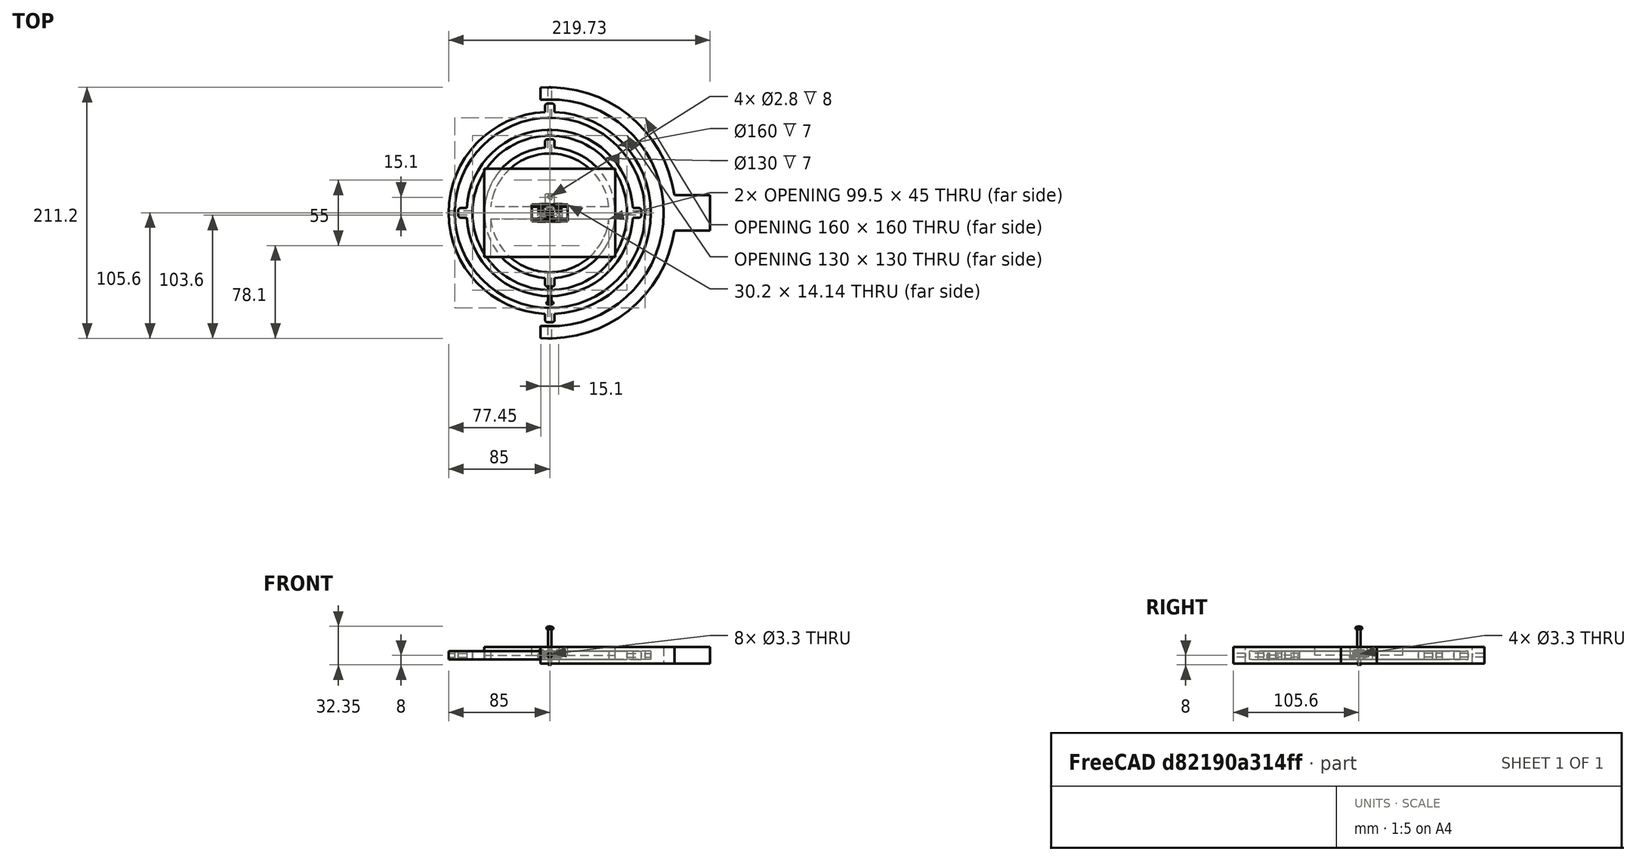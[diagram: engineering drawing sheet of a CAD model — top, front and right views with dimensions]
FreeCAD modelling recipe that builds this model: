
FCSTD DOCUMENT  (FreeCAD 1.1R40006 (Git))
Label: calibration_jig_v1
License: All rights reserved
LicenseURL: https://en.wikipedia.org/wiki/All_rights_reserved
objects: Part::Feature×61, App::Point×18, App::Link×17, App::FeaturePython×15, Sketcher::SketchObject×14, PartDesign::Pad×12, App::Part×11, PartDesign::Pocket×7, PartDesign::Body×6, Part::FeaturePython×4, PartDesign::Fillet×3, App::VarSet×1, PartDesign::Mirrored×1, Assembly::JointGroup×1, Assembly::AssemblyObject×1
note: 167 computed .brp shape members not serialized (recipe doc carries the construction recipe); baked Part::Feature solids carry a one-line shape summary decoded from their .brp

FEATURE [Part::Feature] Part__Feature001  label="PCB"
  shape: bbox 21 x 16 x 1.6 mm, 16 faces (baked)
FEATURE [Part::Feature] Part__Feature002  label="trou1"
  Placement = pos=(-8.89,-6.9,0) rot=(0,0,1;0rad)
  shape: bbox 1.8 x 1.8 x 1.8 mm, 8 faces (baked)
FEATURE [Part::Feature] Part__Feature003  label="trou002"
  Placement = pos=(-6.35,-6.9,0) rot=(0,0,1;0rad)
  shape: bbox 1.8 x 1.8 x 1.8 mm, 8 faces (baked)
FEATURE [Part::Feature] Part__Feature004  label="trou003"
  Placement = pos=(-3.81,-6.9,0) rot=(0,0,1;0rad)
  shape: bbox 1.8 x 1.8 x 1.8 mm, 8 faces (baked)
FEATURE [Part::Feature] Part__Feature005  label="trou004"
  Placement = pos=(-1.27,-6.9,0) rot=(0,0,1;0rad)
  shape: bbox 1.8 x 1.8 x 1.8 mm, 8 faces (baked)
FEATURE [Part::Feature] Part__Feature006  label="trou005"
  Placement = pos=(1.27,-6.9,0) rot=(0,0,1;0rad)
  shape: bbox 1.8 x 1.8 x 1.8 mm, 8 faces (baked)
FEATURE [Part::Feature] Part__Feature007  label="trou006"
  Placement = pos=(3.81,-6.9,0) rot=(0,0,1;0rad)
  shape: bbox 1.8 x 1.8 x 1.8 mm, 8 faces (baked)
FEATURE [Part::Feature] Part__Feature008  label="trou007"
  Placement = pos=(6.35,-6.9,0) rot=(0,0,1;0rad)
  shape: bbox 1.8 x 1.8 x 1.8 mm, 8 faces (baked)
FEATURE [Part::Feature] Part__Feature009  label="trou008"
  Placement = pos=(8.89,-6.9,0) rot=(0,0,1;0rad)
  shape: bbox 1.8 x 1.8 x 1.8 mm, 8 faces (baked)
FEATURE [Part::Feature] Part__Feature010  label="Text_VIN"
  Placement = pos=(-8.45,-3.45,-1.6) rot=(1,0,0;3.14159rad)
  shape: bbox 0.9349 x 0.8597 x 0.05 mm, 11 faces (baked)
FEATURE [Part::Feature] Part__Feature011  label="Text_VIN001"
  Placement = pos=(-8.45,-3.45,-1.6) rot=(1,0,0;3.14159rad)
  shape: bbox 0.9349 x 0.1223 x 0.05 mm, 6 faces (baked)
FEATURE [Part::Feature] Part__Feature012  label="Text_VIN002"
  Placement = pos=(-8.45,-3.45,-1.6) rot=(1,0,0;3.14159rad)
  shape: bbox 0.9349 x 0.7365 x 0.05 mm, 12 faces (baked)
FEATURE [App::Part] Text_VIN  label="Text_VIN003"
  Group = -> [Part__Feature010,Part__Feature011,Part__Feature012]
  Origin = -> Origin
FEATURE [App::Point] Origin001
  Role = Origin
FEATURE [Part::Feature] Part__Feature013  label="Text_3.3V"
  Placement = pos=(-5.81,-2.8,-1.6) rot=(1,0,0;3.14159rad)
  shape: bbox 0.9566 x 0.6115 x 0.05 mm, 32 faces (baked)
FEATURE [Part::Feature] Part__Feature014  label="Text_3.3V001"
  Placement = pos=(-5.81,-2.8,-1.6) rot=(1,0,0;3.14159rad)
  shape: bbox 0.1304 x 0.1304 x 0.05 mm, 6 faces (baked)
FEATURE [Part::Feature] Part__Feature015  label="Text_3.3V002"
  Placement = pos=(-5.81,-2.8,-1.6) rot=(1,0,0;3.14159rad)
  shape: bbox 0.9566 x 0.6115 x 0.05 mm, 32 faces (baked)
FEATURE [Part::Feature] Part__Feature016  label="Text_3.3V003"
  Placement = pos=(-5.81,-2.8,-1.6) rot=(1,0,0;3.14159rad)
  shape: bbox 0.9349 x 0.8597 x 0.05 mm, 11 faces (baked)
FEATURE [App::Part] Text_3_3V  label="Text_3.3V004"
  Group = -> [Part__Feature013,Part__Feature014,Part__Feature015,Part__Feature016]
  Origin = -> Origin002
FEATURE [App::Point] Origin003
  Role = Origin
FEATURE [Part::Feature] Part__Feature017  label="Text_GND"
  Placement = pos=(0.05,-8.35,-1.6) rot=(1,0,0;3.14159rad)
  shape: bbox 0.9675 x 0.8615 x 0.05 mm, 31 faces (baked)
FEATURE [Part::Feature] Part__Feature018  label="Text_GND001"
  Placement = pos=(0.05,-8.35,-1.6) rot=(1,0,0;3.14159rad)
  shape: bbox 0.9349 x 0.7365 x 0.05 mm, 12 faces (baked)
FEATURE [Part::Feature] Part__Feature019  label="Text_GND002"
  Placement = pos=(0.05,-8.35,-1.6) rot=(1,0,0;3.14159rad)
  shape: bbox 0.9349 x 0.7718 x 0.05 mm, 24 faces (baked)
FEATURE [App::Part] Text_GND  label="Text_GND003"
  Group = -> [Part__Feature017,Part__Feature018,Part__Feature019]
  Origin = -> Origin004
FEATURE [App::Point] Origin005
  Role = Origin
FEATURE [Part::Feature] Part__Feature020  label="Text_SCL"
  Placement = pos=(0.2,-8.65,-1.6) rot=(1,0,0;3.14159rad)
  shape: bbox 0.9675 x 0.7392 x 0.05 mm, 37 faces (baked)
FEATURE [Part::Feature] Part__Feature021  label="Text_SCL001"
  Placement = pos=(0.2,-8.65,-1.6) rot=(1,0,0;3.14159rad)
  shape: bbox 0.9675 x 0.8262 x 0.05 mm, 24 faces (baked)
FEATURE [Part::Feature] Part__Feature022  label="Text_SCL002"
  Placement = pos=(0.2,-8.65,-1.6) rot=(1,0,0;3.14159rad)
  shape: bbox 0.9349 x 0.5843 x 0.05 mm, 8 faces (baked)
FEATURE [App::Part] Text_SCL  label="Text_SCL003"
  Group = -> [Part__Feature020,Part__Feature021,Part__Feature022]
  Origin = -> Origin006
FEATURE [App::Point] Origin007
  Role = Origin
FEATURE [Part::Feature] Part__Feature023  label="Text_SDA"
  Placement = pos=(0.2,-8.45,-1.6) rot=(1,0,0;3.14159rad)
  shape: bbox 0.9675 x 0.7392 x 0.05 mm, 37 faces (baked)
FEATURE [Part::Feature] Part__Feature024  label="Text_SDA001"
  Placement = pos=(0.2,-8.45,-1.6) rot=(1,0,0;3.14159rad)
  shape: bbox 0.9349 x 0.7718 x 0.05 mm, 24 faces (baked)
FEATURE [Part::Feature] Part__Feature025  label="Text_SDA002"
  Placement = pos=(0.2,-8.45,-1.6) rot=(1,0,0;3.14159rad)
  shape: bbox 0.9349 x 0.8706 x 0.05 mm, 15 faces (baked)
FEATURE [App::Part] Text_SDA  label="Text_SDA003"
  Group = -> [Part__Feature023,Part__Feature024,Part__Feature025]
  Origin = -> Origin008
FEATURE [App::Point] Origin009
  Role = Origin
FEATURE [Part::Feature] Part__Feature026  label="Text_INT2"
  Placement = pos=(0,-8.4,-1.6) rot=(1,0,0;3.14159rad)
  shape: bbox 0.9349 x 0.1223 x 0.05 mm, 6 faces (baked)
FEATURE [Part::Feature] Part__Feature027  label="Text_INT003"
  Placement = pos=(0,-8.4,-1.6) rot=(1,0,0;3.14159rad)
  shape: bbox 0.9349 x 0.7365 x 0.05 mm, 12 faces (baked)
FEATURE [Part::Feature] Part__Feature028  label="Text_INT004"
  Placement = pos=(0,-8.4,-1.6) rot=(1,0,0;3.14159rad)
  shape: bbox 0.9349 x 0.7365 x 0.05 mm, 10 faces (baked)
FEATURE [Part::Feature] Part__Feature029  label="Text_INT005"
  Placement = pos=(0,-8.4,-1.6) rot=(1,0,0;3.14159rad)
  shape: bbox 0.9403 x 0.6209 x 0.05 mm, 24 faces (baked)
FEATURE [App::Part] Text_INT2  label="Text_INT006"
  Group = -> [Part__Feature026,Part__Feature027,Part__Feature028,Part__Feature029]
  Origin = -> Origin010
FEATURE [App::Point] Origin011
  Role = Origin
FEATURE [Part::Feature] Part__Feature030  label="Text_INT1"
  Placement = pos=(0,-8.6,-1.6) rot=(1,0,0;3.14159rad)
  shape: bbox 0.9349 x 0.1223 x 0.05 mm, 6 faces (baked)
FEATURE [Part::Feature] Part__Feature031  label="Text_INT007"
  Placement = pos=(0,-8.6,-1.6) rot=(1,0,0;3.14159rad)
  shape: bbox 0.9349 x 0.7365 x 0.05 mm, 12 faces (baked)
FEATURE [Part::Feature] Part__Feature032  label="Text_INT008"
  Placement = pos=(0,-8.6,-1.6) rot=(1,0,0;3.14159rad)
  shape: bbox 0.9349 x 0.7365 x 0.05 mm, 10 faces (baked)
FEATURE [Part::Feature] Part__Feature033  label="Text_INT009"
  Placement = pos=(0,-8.6,-1.6) rot=(1,0,0;3.14159rad)
  shape: bbox 0.9403 x 0.3451 x 0.05 mm, 11 faces (baked)
FEATURE [App::Part] Text_INT1  label="Text_INT010"
  Group = -> [Part__Feature030,Part__Feature031,Part__Feature032,Part__Feature033]
  Origin = -> Origin012
FEATURE [App::Point] Origin013
  Role = Origin
FEATURE [Part::Feature] Part__Feature034  label="Text_DRDY"
  Placement = pos=(0,-7.65,-1.6) rot=(1,0,0;3.14159rad)
  shape: bbox 0.9349 x 0.7718 x 0.05 mm, 24 faces (baked)
FEATURE [Part::Feature] Part__Feature035  label="Text_DRDY001"
  Placement = pos=(0,-7.65,-1.6) rot=(1,0,0;3.14159rad)
  shape: bbox 0.9349 x 0.8199 x 0.05 mm, 29 faces (baked)
FEATURE [Part::Feature] Part__Feature036  label="Text_DRDY002"
  Placement = pos=(0,-7.65,-1.6) rot=(1,0,0;3.14159rad)
  shape: bbox 0.9349 x 0.7718 x 0.05 mm, 24 faces (baked)
FEATURE [Part::Feature] Part__Feature037  label="Text_DRDY003"
  Placement = pos=(0,-7.65,-1.6) rot=(1,0,0;3.14159rad)
  shape: bbox 0.9349 x 0.8533 x 0.05 mm, 13 faces (baked)
FEATURE [App::Part] Text_DRDY  label="Text_DRDY004"
  Group = -> [Part__Feature034,Part__Feature035,Part__Feature036,Part__Feature037]
  Origin = -> Origin014
FEATURE [App::Point] Origin015
  Role = Origin
FEATURE [Part::Feature] Part__Feature038  label="R_0603_1608Metric"
  Placement = pos=(-2.45,-1.4,0) rot=(0,0,-1;1.5708rad)
  shape: bbox 0.8 x 1.6 x 0.45 mm, 26 faces (baked)
FEATURE [Part::Feature] Part__Feature039  label="R_0603_1608Metric001"
  Placement = pos=(-1.55,-4.1,0) rot=(0,0,1;0rad)
  shape: bbox 1.6 x 0.8 x 0.45 mm, 26 faces (baked)
FEATURE [Part::Feature] Part__Feature040  label="R_0603_1608Metric002"
  Placement = pos=(1.85,-4.1,0) rot=(0,0,1;3.14159rad)
  shape: bbox 1.6 x 0.8 x 0.45 mm, 26 faces (baked)
FEATURE [Part::Feature] Part__Feature041  label="R_0603_1608Metric003"
  Placement = pos=(2.7,-1.45,0) rot=(0,0,-1;1.5708rad)
  shape: bbox 0.8 x 1.6 x 0.45 mm, 26 faces (baked)
FEATURE [Part::Feature] Part__Feature042  label="C_0603_1608Metric001"
  Placement = pos=(4.2,3.55,0) rot=(0,0,-1;1.5708rad)
  shape: bbox 0.8 x 1.6 x 0.8 mm, 28 faces (baked)
FEATURE [Part::Feature] Part__Feature043  label="C_0603_1608Metric003"
  Placement = pos=(-3.85,5.25,0) rot=(0,0,-1;1.5708rad)
  shape: bbox 0.8 x 1.6 x 0.8 mm, 28 faces (baked)
FEATURE [Part::Feature] Part__Feature044  label="Corps002"
  Placement = pos=(-5.45,-0.65,0.1) rot=(0,0,-1;1.5708rad)
  shape: bbox 1.6 x 3.2 x 2 mm, 8 faces (baked)
FEATURE [Part::Feature] Part__Feature045  label="Corps001 (Mirror #1)"
  Placement = pos=(-1e-15,-1.3,0) rot=(0,0,1;3.14159rad)
  shape: bbox 1 x 0.6 x 1 mm, 8 faces (baked)
FEATURE [Part::Feature] Part__Feature046  label="C_0603_1608Metric004"
  Placement = pos=(-3.85,1.45,0) rot=(0,0,-1;1.5708rad)
  shape: bbox 0.8 x 1.6 x 0.8 mm, 28 faces (baked)
FEATURE [Part::Feature] Part__Feature047  label="C_0603_1608Metric005"
  Placement = pos=(-8.35,-3.5,0) rot=(0,0,1;3.14159rad)
  shape: bbox 1.6 x 0.8 x 0.8 mm, 28 faces (baked)
FEATURE [Part::Feature] Part__Feature048  label="Text_ITGMPU"
  Placement = pos=(-2.3,6.9,-1.6) rot=(0.707107,0.707107,0;3.14159rad)
  shape: bbox 1.034 x 1.161 x 0.05 mm, 31 faces (baked)
FEATURE [Part::Feature] Part__Feature049  label="Text_ITGMPU001"
  Placement = pos=(-2.3,6.9,-1.6) rot=(0.707107,0.707107,0;3.14159rad)
  shape: bbox 1.024 x 1.122 x 0.05 mm, 13 faces (baked)
FEATURE [Part::Feature] Part__Feature050  label="Text_ITGMPU002"
  Placement = pos=(-2.3,6.9,-1.6) rot=(0.707107,0.707107,0;3.14159rad)
  shape: bbox 0.4272 x 0.137 x 0.05 mm, 6 faces (baked)
FEATURE [Part::Feature] Part__Feature051  label="Text_ITGMPU003"
  Placement = pos=(-2.3,6.9,-1.6) rot=(0.707107,0.707107,0;3.14159rad)
  shape: bbox 0.7435 x 1.128 x 0.05 mm, 24 faces (baked)
FEATURE [Part::Feature] Part__Feature052  label="Text_ITGMPU004"
  Placement = pos=(-2.3,6.9,-1.6) rot=(0.707107,0.707107,0;3.14159rad)
  shape: bbox 0.4142 x 1.128 x 0.05 mm, 11 faces (baked)
FEATURE [Part::Feature] Part__Feature053  label="Text_ITGMPU005"
  Placement = pos=(-2.3,6.9,-1.6) rot=(0.707107,0.707107,0;3.14159rad)
  shape: bbox 0.4142 x 1.128 x 0.05 mm, 11 faces (baked)
FEATURE [App::Part] Text_ITGMPU  label="Text_ITGMPU006"
  Group = -> [Part__Feature048,Part__Feature049,Part__Feature050,Part__Feature051,Part__Feature052,Part__Feature053]
  Origin = -> Origin016
FEATURE [App::Point] Origin017
  Role = Origin
FEATURE [Part::Feature] Part__Feature054  label="SOT_23_5"
  Placement = pos=(-8.3,0.05,0) rot=(0,0,1;1.5708rad)
  shape: bbox 2.9 x 2.8 x 1.55 mm, 109 faces (baked)
FEATURE [Part::Feature] Part__Feature055  label="Text_XYZ"
  Placement = pos=(3.5,-0.7,0) rot=(0,0,1;0rad)
  shape: bbox 2.812 x 2.484 x 0.05 mm, 16 faces (baked)
FEATURE [Part::Feature] Part__Feature056  label="Text_XYZ001"
  Placement = pos=(3.5,-0.7,0) rot=(0,0,1;0rad)
  shape: bbox 1.038 x 0.6722 x 0.05 mm, 10 faces (baked)
FEATURE [Part::Feature] Part__Feature057  label="Text_XYZ002"
  Placement = pos=(3.5,-0.7,0) rot=(0,0,1;0rad)
  shape: bbox 1.038 x 0.6722 x 0.05 mm, 14 faces (baked)
FEATURE [Part::Feature] Part__Feature058  label="Text_XYZ003"
  Placement = pos=(3.5,-0.7,0) rot=(0,0,1;0rad)
  shape: bbox 1.038 x 0.6722 x 0.05 mm, 11 faces (baked)
FEATURE [App::Part] Text_XYZ  label="Text_XYZ004"
  Group = -> [Part__Feature055,Part__Feature056,Part__Feature057,Part__Feature058]
  Origin = -> Origin018
FEATURE [App::Point] Origin019
  Role = Origin
FEATURE [Part::Feature] Part__Feature059  label="LGA_14_3x5mm_P08mm_LayoutBorder1x6y"
  Placement = pos=(-1e-15,3.9,0) rot=(0,0,1;1.5708rad)
  shape: bbox 5 x 3 x 0.78 mm, 78 faces (baked)
FEATURE [Part::Feature] Part__Feature060  label="SOT_363_SC_70_6"
  Placement = pos=(0,-1.45,0) rot=(0,0,1;0rad)
  shape: bbox 2 x 2 x 1.05 mm, 118 faces (baked)
FEATURE [Part::Feature] Part__Feature061  label="Corps001"
  Placement = pos=(-5.45,-0.65,0) rot=(0,0,1;1.5708rad)
  shape: bbox 1 x 0.6 x 1 mm, 8 faces (baked)
FEATURE [App::Part] GY_511_LSM303DLHC
  Group = -> [Part__Feature001,Part__Feature002,Part__Feature003,Part__Feature004,Part__Feature005,Part__Feature006,Part__Feature007,Part__Feature008,Part__Feature009,Text_VIN,Text_3_3V,Text_GND,Text_SCL,Text_SDA,Text_INT2,Text_INT1,Text_DRDY,Part__Feature038,Part__Feature039,Part__Feature040,Part__Feature041,Part__Feature042,Part__Feature043,Part__Feature044,Part__Feature045,Part__Feature046,Part__Feature047,+6 more]
  Origin = -> Origin020
FEATURE [App::Point] Origin021
  Role = Origin
FEATURE [App::Point] Origin023
  Role = Origin
FEATURE [App::VarSet] VarSet
  Base_ring_base_diameter = 95.6
  Base_ring_connector_lenght = 8
  Base_ring_connector_scew = 3.3
  Base_ring_connector_width = 12
  Base_ring_depth = 7
  Base_ring_width = 10
  Base_second_ring_diameter = 130
  Base_sensor_base_diameter = 100
  Base_third_ring_diameter = 160
  expr: Base_ring_base_diameter = (Base_sensor_base_diameter + 6.6 * Base_ring_connector_width + 1.2 * Base_ring_width) / 2
  expr: Base_second_ring_diameter = Base_sensor_base_diameter + 1.5 * Base_ring_connector_width + 1.2 * Base_ring_width
  expr: Base_third_ring_diameter = Base_sensor_base_diameter + 4 * Base_ring_connector_width + 1.2 * Base_ring_width
FEATURE [Sketcher::SketchObject] Sketch
  ArcFitTolerance = 1e-06
  AttachmentSupport = -> [XY_Plane011]
  ExternalTypes = [0]
  FullyConstrained = true
  MakeInternals = false
  MapMode = 5
  expr: Constraints[2] = VarSet.Base_sensor_base_diameter
  expr: Constraints[3] = VarSet.Base_sensor_base_diameter + VarSet.Base_ring_width
  sketch-geometry (2):
    g0: Circle CenterX=0 CenterY=0 CenterZ=0 NormalX=0 NormalY=0 NormalZ=1 AngleXU=0 Radius=55
    g1: Circle CenterX=0 CenterY=0 CenterZ=0 NormalX=0 NormalY=0 NormalZ=1 AngleXU=0 Radius=50
  constraints (5):
    c: Coincident(g0,g-1)
    c: PointOnObject(g1,g-2)
    c: Diameter(g1) = 100
    c: Diameter(g0) = 110
    c: PointOnObject(g1,g-1)
FEATURE [PartDesign::Pad] Pad002
  Direction = (0,0,1)
  Length = 7
  Length2 = 10
  Midplane = true
  Profile = -> Sketch
  ReferenceAxis = -> Sketch [N_Axis]
  Refine = true
  Suppressed = false
  Type = 0
  expr: Length = VarSet.Base_ring_depth
FEATURE [Sketcher::SketchObject] Sketch069
  ArcFitTolerance = 1e-06
  AttachmentSupport = -> [XY_Plane011]
  ExternalTypes = [0]
  FullyConstrained = true
  MakeInternals = false
  MapMode = 5
  expr: Constraints[10] = VarSet.Base_sensor_base_diameter / 2
  expr: Constraints[7] = VarSet.Base_ring_connector_lenght
  expr: Constraints[8] = VarSet.Base_ring_connector_width
  sketch-geometry (4):
    g0: LineSegment StartX=-4 StartY=62 StartZ=0 EndX=-4 EndY=50 EndZ=0
    g1: LineSegment StartX=-4 StartY=50 StartZ=0 EndX=4 EndY=50 EndZ=0
    g2: LineSegment StartX=4 StartY=50 StartZ=0 EndX=4 EndY=62 EndZ=0
    g3: LineSegment StartX=4 StartY=62 StartZ=0 EndX=-4 EndY=62 EndZ=0
  constraints (11):
    c: Coincident(g0,g1)
    c: Coincident(g1,g2)
    c: Coincident(g2,g3)
    c: Coincident(g3,g0)
    c: Vertical(g0)
    c: Vertical(g2)
    c: Horizontal(g1)
    c: Distance(g0,g2) = 8
    c: Distance(g1,g3) = 12
    c: Symmetric(g0,g2,g-2)
    c: DistanceY(g-1,g1) = 50
FEATURE [PartDesign::Pad] Pad003
  BaseFeature = -> Pad002
  Direction = (0,0,1)
  Length = 7
  Length2 = 10
  Midplane = true
  Profile = -> Sketch069
  ReferenceAxis = -> Sketch069 [N_Axis]
  Refine = true
  Suppressed = false
  Type = 0
  expr: Length = VarSet.Base_ring_depth
FEATURE [PartDesign::Mirrored] Mirrored
  BaseFeature = -> Pad003
  MirrorPlane = -> Sketch069 [H_Axis]
  Originals = -> [Pad003]
  Refine = true
  Suppressed = false
  TransformMode = 0
FEATURE [App::Point] Origin087
  Role = Origin
FEATURE [Sketcher::SketchObject] Sketch071
  ArcFitTolerance = 1e-06
  AttachmentSupport = -> [XY_Plane046]
  ExternalTypes = [0]
  FullyConstrained = true
  MakeInternals = false
  MapMode = 5
  expr: Constraints[13] = VarSet.Base_ring_connector_width
  expr: Constraints[14] = VarSet.Base_ring_connector_lenght
  expr: Constraints[2] = VarSet.Base_second_ring_diameter
  expr: Constraints[3] = VarSet.Base_second_ring_diameter + VarSet.Base_ring_width
  sketch-geometry (10):
    g0: Circle CenterX=0 CenterY=0 CenterZ=0 NormalX=0 NormalY=0 NormalZ=1 AngleXU=0 Radius=70
    g1: Circle CenterX=0 CenterY=0 CenterZ=0 NormalX=0 NormalY=0 NormalZ=1 AngleXU=0 Radius=65
    g2: LineSegment StartX=65 StartY=4 StartZ=0 EndX=65 EndY=-4 EndZ=0
    g3: LineSegment StartX=65 StartY=-4 StartZ=0 EndX=77 EndY=-4 EndZ=0
    g4: LineSegment StartX=77 StartY=-4 StartZ=0 EndX=77 EndY=4 EndZ=0
    g5: LineSegment StartX=77 StartY=4 StartZ=0 EndX=65 EndY=4 EndZ=0
    g6: LineSegment StartX=-77 StartY=4 StartZ=0 EndX=-65 EndY=4 EndZ=0
    g7: LineSegment StartX=-65 StartY=4 StartZ=0 EndX=-65 EndY=-4 EndZ=0
    g8: LineSegment StartX=-65 StartY=-4 StartZ=0 EndX=-77 EndY=-4 EndZ=0
    g9: LineSegment StartX=-77 StartY=-4 StartZ=0 EndX=-77 EndY=4 EndZ=0
  constraints (26):
    c: Coincident(g0,g-1)
    c: Coincident(g1,g0)
    c: Diameter(g1) = 130
    c: Diameter(g0) = 140
    c: Coincident(g2,g3)
    c: Coincident(g3,g4)
    c: Coincident(g4,g5)
    c: Coincident(g5,g2)
    c: Vertical(g4)
    c: Horizontal(g3)
    c: Horizontal(g5)
    c: Symmetric(g2,g2,g-1)
    c: Tangent(g2,g1)
    c: DistanceX(g2,g3) = 12
    c: DistanceY(g3,g4) = 8
    c: Coincident(g7,g8)
    c: Coincident(g8,g9)
    c: Coincident(g9,g6)
    c: Coincident(g6,g7)
    c: Vertical(g9)
    c: Horizontal(g8)
    c: Horizontal(g6)
    c: Equal(g3,g8)
    c: Equal(g9,g4)
    c: Symmetric(g7,g6,g-1)
    c: Tangent(g7,g1)
FEATURE [PartDesign::Pad] Pad004
  Direction = (0,0,1)
  Length = 7
  Length2 = 10
  Midplane = true
  Profile = -> Sketch071 [Edge1,Edge2]
  ReferenceAxis = -> Sketch071 [N_Axis]
  Refine = true
  Suppressed = false
  Type = 0
  expr: Length = VarSet.Base_ring_depth
FEATURE [PartDesign::Pad] Pad005
  BaseFeature = -> Pad004
  Direction = (0,0,1)
  Length = 7
  Length2 = 10
  Midplane = true
  Profile = -> Sketch071 [Edge7,Edge8,Edge9,Edge10,Edge3,Edge6,Edge5,Edge4]
  ReferenceAxis = -> Sketch071 [N_Axis]
  Refine = true
  Suppressed = false
  Type = 0
  expr: Length = VarSet.Base_ring_depth
FEATURE [Sketcher::SketchObject] Sketch073
  ArcFitTolerance = 1e-06
  AttachmentSupport = -> [XZ_Plane046]
  ExternalTypes = [0]
  FullyConstrained = true
  MakeInternals = false
  MapMode = 5
  Placement = pos=(0,0,0) rot=(1,0,0;1.5708rad)
  expr: Constraints[1] = VarSet.Base_ring_connector_scew
  sketch-geometry (1):
    g0: Circle CenterX=0 CenterY=0 CenterZ=0 NormalX=0 NormalY=0 NormalZ=1 AngleXU=0 Radius=1.65
  constraints (2):
    c: Coincident(g0,g-1)
    c: Diameter(g0) = 3.3
FEATURE [PartDesign::Pocket] Pocket003
  BaseFeature = -> Pad005
  Direction = (0,1,-2e-16)
  Length = 5
  Length2 = 5
  Midplane = true
  Profile = -> Sketch073
  ReferenceAxis = -> Sketch073 [N_Axis]
  Refine = true
  Suppressed = false
  Type = 1
FEATURE [App::Point] Origin089
  Role = Origin
FEATURE [Sketcher::SketchObject] Sketch074
  ArcFitTolerance = 1e-06
  AttachmentSupport = -> [XY_Plane047]
  ExternalTypes = [0]
  FullyConstrained = true
  MakeInternals = false
  MapMode = 5
  expr: Constraints[12] = VarSet.Base_ring_connector_lenght
  expr: Constraints[13] = VarSet.Base_ring_connector_width
  expr: Constraints[1] = VarSet.Base_third_ring_diameter
  expr: Constraints[23] = VarSet.Base_ring_connector_width
  expr: Constraints[24] = VarSet.Base_ring_connector_lenght
  expr: Constraints[2] = VarSet.Base_third_ring_diameter + VarSet.Base_ring_width
  sketch-geometry (10):
    g0: Circle CenterX=0 CenterY=0 CenterZ=0 NormalX=0 NormalY=0 NormalZ=1 AngleXU=0 Radius=85
    g1: Circle CenterX=0 CenterY=0 CenterZ=0 NormalX=0 NormalY=0 NormalZ=1 AngleXU=0 Radius=80
    g2: LineSegment StartX=-4 StartY=92 StartZ=0 EndX=-4 EndY=80 EndZ=0
    g3: LineSegment StartX=-4 StartY=80 StartZ=0 EndX=4 EndY=80 EndZ=0
    g4: LineSegment StartX=4 StartY=80 StartZ=0 EndX=4 EndY=92 EndZ=0
    g5: LineSegment StartX=4 StartY=92 StartZ=0 EndX=-4 EndY=92 EndZ=0
    g6: LineSegment StartX=-4 StartY=-80 StartZ=0 EndX=-4 EndY=-92 EndZ=0
    g7: LineSegment StartX=-4 StartY=-92 StartZ=0 EndX=4 EndY=-92 EndZ=0
    g8: LineSegment StartX=4 StartY=-92 StartZ=0 EndX=4 EndY=-80 EndZ=0
    g9: LineSegment StartX=4 StartY=-80 StartZ=0 EndX=-4 EndY=-80 EndZ=0
  constraints (26):
    c: Coincident(g1,g0)
    c: Diameter(g1) = 160
    c: Diameter(g0) = 170
    c: Coincident(g0,g-1)
    c: Coincident(g2,g3)
    c: Coincident(g3,g4)
    c: Coincident(g4,g5)
    c: Coincident(g5,g2)
    c: Vertical(g2)
    c: Vertical(g4)
    c: Horizontal(g5)
    c: Symmetric(g2,g3,g-2)
    c: DistanceX(g2,g3) = 8
    c: DistanceY(g3,g4) = 12
    c: Tangent(g3,g1)
    c: Coincident(g6,g7)
    c: Coincident(g7,g8)
    c: Coincident(g8,g9)
    c: Coincident(g9,g6)
    c: Vertical(g6)
    c: Vertical(g8)
    c: Horizontal(g9)
    c: Symmetric(g7,g6,g-2)
    c: DistanceY(g6,g6) = 12
    c: DistanceX(g6,g8) = 8
    c: Tangent(g9,g1)
FEATURE [Sketcher::SketchObject] Sketch075
  ArcFitTolerance = 1e-06
  AttachmentSupport = -> [XZ_Plane047]
  ExternalTypes = [0]
  FullyConstrained = true
  MakeInternals = false
  MapMode = 5
  Placement = pos=(0,0,0) rot=(1,0,0;1.5708rad)
  expr: Constraints[1] = VarSet.Base_ring_connector_scew
  sketch-geometry (1):
    g0: Circle CenterX=0 CenterY=0 CenterZ=0 NormalX=0 NormalY=0 NormalZ=1 AngleXU=0 Radius=1.65
  constraints (2):
    c: Coincident(g0,g-1)
    c: Diameter(g0) = 3.3
FEATURE [Sketcher::SketchObject] Sketch076
  ArcFitTolerance = 1e-06
  AttachmentSupport = -> [YZ_Plane047]
  ExternalTypes = [0]
  FullyConstrained = true
  MakeInternals = false
  MapMode = 5
  Placement = pos=(0,0,0) rot=(0.57735,0.57735,0.57735;2.0944rad)
  expr: Constraints[1] = VarSet.Base_ring_connector_scew
  sketch-geometry (1):
    g0: Circle CenterX=0 CenterY=0 CenterZ=0 NormalX=0 NormalY=0 NormalZ=1 AngleXU=0 Radius=1.65
  constraints (2):
    c: Coincident(g0,g-1)
    c: Diameter(g0) = 3.3
FEATURE [PartDesign::Pad] Pad006
  Direction = (0,0,1)
  Length = 7
  Length2 = 10
  Midplane = true
  Profile = -> Sketch074 [Edge2,Edge1]
  ReferenceAxis = -> Sketch074 [N_Axis]
  Refine = true
  Suppressed = false
  Type = 0
  expr: Length = VarSet.Base_ring_depth
FEATURE [PartDesign::Pad] Pad007
  BaseFeature = -> Pad006
  Direction = (0,0,1)
  Length = 7
  Length2 = 10
  Midplane = true
  Profile = -> Sketch074 [Edge4,Edge3,Edge5,Edge6,Edge10,Edge7,Edge8,Edge9]
  ReferenceAxis = -> Sketch074 [N_Axis]
  Refine = true
  Suppressed = false
  Type = 0
  expr: Length = VarSet.Base_ring_depth
FEATURE [PartDesign::Pocket] Pocket004
  BaseFeature = -> Pad007
  Direction = (-1,0,0)
  Length = 5
  Length2 = 5
  Midplane = true
  Profile = -> Sketch076
  ReferenceAxis = -> Sketch076 [N_Axis]
  Refine = true
  Suppressed = false
  Type = 1
FEATURE [PartDesign::Pocket] Pocket005
  BaseFeature = -> Pocket004
  Direction = (0,1,-2e-16)
  Length = 5
  Length2 = 5
  Midplane = true
  Profile = -> Sketch075
  ReferenceAxis = -> Sketch075 [N_Axis]
  Refine = true
  Suppressed = false
  Type = 1
FEATURE [App::Point] Origin091
  Role = Origin
FEATURE [Sketcher::SketchObject] Sketch077
  ArcFitTolerance = 1e-06
  AttachmentSupport = -> [XY_Plane048]
  ExternalTypes = [0]
  FullyConstrained = true
  MakeInternals = false
  MapMode = 5
  expr: Constraints[11] = 3 * VarSet.Base_ring_width
  expr: Constraints[20] = VarSet.Base_ring_base_diameter
  expr: Constraints[7] = VarSet.Base_ring_width
  sketch-geometry (15):
    g0: ArcOfCircle CenterX=0.199246 CenterY=2.76e-14 CenterZ=0 NormalX=0 NormalY=0 NormalZ=1 AngleXU=0 Radius=105.6 StartAngle=0.142528 EndAngle=1.64852
    g1: ArcOfCircle CenterX=0.199246 CenterY=2.05388e-11 CenterZ=0 NormalX=0 NormalY=0 NormalZ=1 AngleXU=0 Radius=105.6 StartAngle=4.63467 EndAngle=6.14066
    g2: LineSegment StartX=-8 StartY=105.281 StartZ=0 EndX=-8 EndY=95.2812 EndZ=0
    g3: LineSegment StartX=-8 StartY=-105.281 StartZ=0 EndX=-8 EndY=-95.2812 EndZ=0
    g4: LineSegment [constr] StartX=-8 StartY=-105.281 StartZ=0 EndX=-8 EndY=105.281 EndZ=0
    g5: LineSegment StartX=104.728 StartY=-15 StartZ=0 EndX=134.728 EndY=-15 EndZ=0
    g6: LineSegment StartX=134.728 StartY=-15 StartZ=0 EndX=134.728 EndY=15 EndZ=0
    g7: LineSegment StartX=134.728 StartY=15 StartZ=0 EndX=104.728 EndY=15 EndZ=0
    g8: LineSegment [constr] StartX=134.728 StartY=-15 StartZ=0 EndX=104.728 EndY=-15 EndZ=0
    g9: LineSegment [constr] StartX=134.728 StartY=15 StartZ=0 EndX=104.728 EndY=15 EndZ=0
    g10: ArcOfCircle CenterX=0.199246 CenterY=2.76e-14 CenterZ=0 NormalX=0 NormalY=0 NormalZ=1 AngleXU=0 Radius=95.6 StartAngle=4.79408 EndAngle=7.77229
    g11: LineSegment StartX=-8 StartY=-95.2812 StartZ=0 EndX=8 EndY=-95.2812 EndZ=0
    g12: LineSegment StartX=-8 StartY=95.2812 StartZ=0 EndX=8 EndY=95.2812 EndZ=0
    g13: LineSegment [constr] StartX=8 StartY=95.2812 StartZ=0 EndX=8 EndY=-95.2812 EndZ=0
    g14: LineSegment [constr] StartX=104.728 StartY=-15 StartZ=0 EndX=104.728 EndY=15 EndZ=0
  constraints (40):
    c: Coincident(g2,g0)
    c: Coincident(g3,g1)
    c: Coincident(g4,g1)
    c: Coincident(g4,g0)
    c: Vertical(g4)
    c: PointOnObject(g2,g4)
    c: Distance(g4,g-2) = 8
    c: DistanceY(g2,g0) = 10
    c: Equal(g3,g2)
    c: Coincident(g5,g6)
    c: Coincident(g6,g7)
    c: DistanceY(g5,g6) = 30
    c: Distance(g8,g5) = 30
    c: Horizontal(g5)
    c: Coincident(g1,g5)
    c: Horizontal(g7)
    c: Coincident(g0,g7)
    c: Coincident(g8,g5)
    c: Coincident(g9,g6)
    c: Coincident(g10,g0)
    c: Radius(g10) = 95.6
    c: Coincident(g11,g3)
    c: Coincident(g11,g10)
    c: Horizontal(g11)
    c: Coincident(g12,g2)
    c: Coincident(g12,g10)
    c: Horizontal(g12)
    c: Coincident(g13,g10)
    c: Coincident(g13,g10)
    c: Vertical(g13)
    c: Distance(g13,g4) = 16
    c: Symmetric(g5,g6,g-1)
    c: Coincident(g8,g1)
    c: Coincident(g14,g1)
    c: Coincident(g14,g0)
    c: Vertical(g14)
    c: Coincident(g9,g0)
    c: Symmetric(g2,g3,g-1)
    c: Distance(g0,g10) = 10
    c: Equal(g1,g0)
FEATURE [PartDesign::Pad] Pad008
  Direction = (0,0,1)
  Length = 14
  Length2 = 10
  Midplane = true
  Profile = -> Sketch077
  ReferenceAxis = -> Sketch077 [N_Axis]
  Refine = true
  Suppressed = false
  Type = 0
  expr: Length = 2 * VarSet.Base_ring_depth
FEATURE [App::Point] Origin093
  Role = Origin
FEATURE [Sketcher::SketchObject] Sketch078
  ArcFitTolerance = 1e-06
  AttachmentSupport = -> [XY_Plane049]
  ExternalTypes = [0]
  FullyConstrained = true
  MakeInternals = false
  MapMode = 5
  expr: Constraints[20] = 2.02 * VarSet.Base_ring_depth
  expr: Constraints[21] = 3.02 * VarSet.Base_ring_width
  sketch-geometry (10):
    g0: LineSegment StartX=-15.1 StartY=7.07 StartZ=0 EndX=-15.1 EndY=-7.07 EndZ=0
    g1: LineSegment StartX=-15.1 StartY=-7.07 StartZ=0 EndX=15.1 EndY=-7.07 EndZ=0
    g2: LineSegment StartX=15.1 StartY=-7.07 StartZ=0 EndX=15.1 EndY=7.07 EndZ=0
    g3: LineSegment StartX=15.1 StartY=7.07 StartZ=0 EndX=-15.1 EndY=7.07 EndZ=0
    g4: GeomPoint [constr] X=0 Y=0 Z=0
    g5: LineSegment StartX=-55.1 StartY=37.07 StartZ=0 EndX=-55.1 EndY=-37.07 EndZ=0
    g6: LineSegment StartX=-55.1 StartY=-37.07 StartZ=0 EndX=55.1 EndY=-37.07 EndZ=0
    g7: LineSegment StartX=55.1 StartY=-37.07 StartZ=0 EndX=55.1 EndY=37.07 EndZ=0
    g8: LineSegment StartX=55.1 StartY=37.07 StartZ=0 EndX=-55.1 EndY=37.07 EndZ=0
    g9: GeomPoint [constr] X=0 Y=0 Z=0
  constraints (24):
    c: Coincident(g0,g1)
    c: Coincident(g1,g2)
    c: Coincident(g2,g3)
    c: Coincident(g3,g0)
    c: Vertical(g0)
    c: Vertical(g2)
    c: Horizontal(g1)
    c: Horizontal(g3)
    c: Symmetric(g2,g0,g4)
    c: Coincident(g4,g-1)
    c: Coincident(g5,g6)
    c: Coincident(g6,g7)
    c: Coincident(g7,g8)
    c: Coincident(g8,g5)
    c: Vertical(g5)
    c: Vertical(g7)
    c: Horizontal(g6)
    c: Horizontal(g8)
    c: Symmetric(g7,g5,g9)
    c: Coincident(g9,g4)
    c: DistanceY(g1,g2) = 14.14
    c: DistanceX(g0,g2) = 30.2
    c: DistanceX(g5,g0) = 40
    c: DistanceY(g0,g5) = 30
FEATURE [PartDesign::Pad] Pad009
  Direction = (0,0,1)
  Length = 7
  Length2 = 10
  Profile = -> Sketch078
  ReferenceAxis = -> Sketch078 [N_Axis]
  Refine = true
  Suppressed = false
  Type = 0
  expr: Length = VarSet.Base_ring_depth
FEATURE [PartDesign::Body] Body024  label="base"
  AllowCompound = false
  Group = -> [Sketch078,Pad009]
  Origin = -> Origin092
  Tip = -> Pad009
FEATURE [Sketcher::SketchObject] Sketch079
  ArcFitTolerance = 1e-06
  AttachmentSupport = -> [XZ_Plane048]
  ExternalTypes = [0]
  FullyConstrained = true
  MakeInternals = false
  MapMode = 5
  Placement = pos=(0,0,0) rot=(1,0,0;1.5708rad)
  expr: Constraints[1] = VarSet.Base_ring_connector_scew
  sketch-geometry (1):
    g0: Circle CenterX=0 CenterY=0 CenterZ=0 NormalX=0 NormalY=0 NormalZ=1 AngleXU=0 Radius=1.65
  constraints (2):
    c: Coincident(g0,g-1)
    c: Diameter(g0) = 3.3
FEATURE [PartDesign::Pocket] Pocket006
  BaseFeature = -> Pad008
  Direction = (0,1,-2e-16)
  Length = 5
  Length2 = 5
  Midplane = true
  Profile = -> Sketch079
  ReferenceAxis = -> Sketch079 [N_Axis]
  Refine = true
  Suppressed = false
  Type = 1
FEATURE [PartDesign::Body] Body023  label="base_outside"
  AllowCompound = false
  Group = -> [Sketch077,Pad008,Sketch079,Pocket006]
  Origin = -> Origin090
  Tip = -> Pocket006
FEATURE [App::Point] Origin095
  Role = Origin
FEATURE [Sketcher::SketchObject] Sketch080
  ArcFitTolerance = 1e-06
  AttachmentSupport = -> [XY_Plane050]
  ExternalTypes = [0]
  FullyConstrained = true
  MakeInternals = false
  MapMode = 5
  expr: Constraints[2] = VarSet.Base_ring_connector_scew
  sketch-geometry (2):
    g0: Circle CenterX=0 CenterY=0 CenterZ=0 NormalX=0 NormalY=0 NormalZ=1 AngleXU=0 Radius=1.65
    g1: Circle CenterX=0 CenterY=0 CenterZ=0 NormalX=0 NormalY=0 NormalZ=1 AngleXU=0 Radius=3.65
  constraints (4):
    c: Coincident(g0,g-1)
    c: Coincident(g1,g0)
    c: Diameter(g0) = 3.3
    c: Distance(g0,g1) = 2
FEATURE [PartDesign::Pad] Pad010
  Direction = (0,0,1)
  Length = 2
  Length2 = 10
  Midplane = true
  Profile = -> Sketch080
  ReferenceAxis = -> Sketch080 [N_Axis]
  Refine = true
  Suppressed = false
  Type = 0
FEATURE [PartDesign::Body] Body025  label="space"
  AllowCompound = false
  Group = -> [Sketch080,Pad010]
  Origin = -> Origin094
  Tip = -> Pad010
FEATURE [App::Point] Origin097
  Role = Origin
FEATURE [App::Link] base  label="base001"
  LinkedObject = -> Body024
FEATURE [App::FeaturePython] GroundedJoint  # Assembly grounded joint (typed FeaturePython)
  ObjectToGround = -> base
FEATURE [App::Link] base_outside  label="base_outside001"
  LinkPlacement = pos=(-2.6e-15,14.07,134.728) rot=(0.57735,0.57735,-0.57735;2.0944rad)
  LinkedObject = -> Body023
  Placement = pos=(-2.6e-15,14.07,134.728) rot=(0.57735,0.57735,-0.57735;2.0944rad)
FEATURE [App::Link] space  label="space001"
  LinkPlacement = pos=(94.4373,14.07,134.728) rot=(0.707107,0,-0.707107;3.14159rad)
  LinkedObject = -> Body025
  Placement = pos=(94.4373,14.07,134.728) rot=(0.707107,0,-0.707107;3.14159rad)
FEATURE [App::Link] third_circle  label="third_circle001"
  LinkPlacement = pos=(1.43729,14.07,134.728) rot=(0.57735,0.57735,-0.57735;2.0944rad)
  LinkedObject = -> Body022
  Placement = pos=(1.43729,14.07,134.728) rot=(0.57735,0.57735,-0.57735;2.0944rad)
FEATURE [App::Link] space001  label="space006"
  LinkPlacement = pos=(1.43729,14.07,213.22) rot=(0,0,1;0rad)
  LinkedObject = -> Body025
  Placement = pos=(1.43729,14.07,213.22) rot=(0,0,1;0rad)
FEATURE [App::Link] space002  label="space003"
  LinkPlacement = pos=(80.5115,1.7298,121.104) rot=(-0.384867,0.643615,0.661542;1.87625rad)
  LinkedObject = -> Body025
  Placement = pos=(80.5115,1.7298,121.104) rot=(-0.384867,0.643615,0.661542;1.87625rad)
FEATURE [App::Link] space003  label="space004"
  LinkPlacement = pos=(-62.0526,14.07,135.22) rot=(0,1,0;4.71239rad)
  LinkedObject = -> Body025
  Placement = pos=(-62.0526,14.07,135.22) rot=(0,1,0;4.71239rad)
FEATURE [App::Link] second_cicle  label="second_cicle001"
  LinkPlacement = pos=(1.43729,14.07,135.22) rot=(0.57735,0.57735,0.57735;4.18879rad)
  LinkedObject = -> Body021
  Placement = pos=(1.43729,14.07,135.22) rot=(0.57735,0.57735,0.57735;4.18879rad)
FEATURE [App::Link] first_circle  label="first_circle001"
  LinkPlacement = pos=(0.947386,14.07,135.22) rot=(-0.57735,0.57735,-0.57735;4.18879rad)
  LinkedObject = -> Body
  Placement = pos=(0.947386,14.07,135.22) rot=(-0.57735,0.57735,-0.57735;4.18879rad)
FEATURE [App::Link] space004  label="space005"
  LinkPlacement = pos=(89.3064,-1.573,115.544) rot=(0.56245,0.669832,-0.484742;3.28422rad)
  LinkedObject = -> Body025
  Placement = pos=(89.3064,-1.573,115.544) rot=(0.56245,0.669832,-0.484742;3.28422rad)
FEATURE [Sketcher::SketchObject] Sketch081  label="sensor_base"
  ArcFitTolerance = 1e-06
  AttachmentSupport = -> [XY_Plane011]
  ExternalTypes = [0]
  FullyConstrained = true
  MakeInternals = false
  MapMode = 5
  expr: Constraints[20] = VarSet.Base_sensor_base_diameter * 1.1
  sketch-geometry (18):
    g0: Circle CenterX=7.55 CenterY=2.4 CenterZ=0 NormalX=0 NormalY=0 NormalZ=1 AngleXU=0 Radius=1.4
    g1: Circle CenterX=-7.55 CenterY=2.4 CenterZ=0 NormalX=0 NormalY=0 NormalZ=1 AngleXU=0 Radius=1.4
    g2: Circle CenterX=-7.55 CenterY=2.4 CenterZ=0 NormalX=0 NormalY=0 NormalZ=1 AngleXU=0 Radius=2.2
    g3: Circle CenterX=7.55 CenterY=2.4 CenterZ=0 NormalX=0 NormalY=0 NormalZ=1 AngleXU=0 Radius=2.2
    g4: GeomPoint X=-1e-16 Y=2.4 Z=0
    g5: LineSegment [constr] StartX=-1e-16 StartY=2.4 StartZ=0 EndX=-1e-16 EndY=-1.6 EndZ=0
    g6: LineSegment StartX=-55 StartY=-5 StartZ=0 EndX=55 EndY=-5 EndZ=0
    g7: LineSegment StartX=55 StartY=5 StartZ=0 EndX=-55 EndY=5 EndZ=0
    g8: Circle CenterX=0 CenterY=-2 CenterZ=0 NormalX=0 NormalY=0 NormalZ=1 AngleXU=0 Radius=2.2
    g9: LineSegment StartX=-55 StartY=5 StartZ=0 EndX=-55 EndY=-5 EndZ=0
    g10: LineSegment StartX=55 StartY=-5 StartZ=0 EndX=55 EndY=5 EndZ=0
    g11: Circle CenterX=0 CenterY=-2 CenterZ=0 NormalX=0 NormalY=0 NormalZ=1 AngleXU=0 Radius=1.4
    g12: Circle CenterX=0 CenterY=13.1 CenterZ=0 NormalX=0 NormalY=0 NormalZ=1 AngleXU=0 Radius=1.4
    g13: Circle CenterX=0 CenterY=13.1 CenterZ=0 NormalX=0 NormalY=0 NormalZ=1 AngleXU=0 Radius=2.2
    g14: LineSegment StartX=-4 StartY=16 StartZ=0 EndX=-4 EndY=4 EndZ=0
    g15: LineSegment StartX=-4 StartY=4 StartZ=0 EndX=4 EndY=4 EndZ=0
    g16: LineSegment StartX=4 StartY=4 StartZ=0 EndX=4 EndY=16 EndZ=0
    g17: LineSegment StartX=4 StartY=16 StartZ=0 EndX=-4 EndY=16 EndZ=0
  constraints (44):
    c: Diameter(g1) = 2.8
    c: Coincident(g2,g1)
    c: Coincident(g3,g0)
    c: Equal(g1,g0)
    c: Diameter(g2) = 4.4
    c: Equal(g2,g3)
    c: DistanceX(g1,g0) = 15.1
    c: Symmetric(g1,g0,g4)
    c: Coincident(g5,g4)
    c: Vertical(g5)
    c: DistanceY(g5,g1) = 4
    c: Horizontal(g7)
    c: Symmetric(g6,g6,g-2)
    c: DistanceY(g6,g7) = 10
    c: Symmetric(g6,g7,g-1)
    c: PointOnObject(g8,g-2)
    c: Equal(g3,g8)
    c: Distance(g-1,g8) = 2
    c: Symmetric(g1,g0,g-2)
    c: Distance(g3,g7) = 0.4
    c: DistanceX(g6,g6) = 110
    c: Coincident(g9,g7)
    c: Coincident(g9,g6)
    c: Coincident(g10,g6)
    c: Coincident(g10,g7)
    c: Vertical(g10)
    c: Coincident(g11,g8)
    c: PointOnObject(g12,g-2)
    c: Coincident(g13,g12)
    c: Equal(g8,g13)
    c: Equal(g1,g11)
    c: Equal(g11,g12)
    c: Distance(g8,g12) = 15.1
    c: Coincident(g14,g15)
    c: Coincident(g15,g16)
    c: Coincident(g16,g17)
    c: Coincident(g17,g14)
    c: Vertical(g14)
    c: Vertical(g16)
    c: Horizontal(g15)
    c: Symmetric(g14,g16,g-2)
    c: DistanceX(g14,g16) = 8
    c: Distance(g15,g7) = 1
    c: DistanceY(g15,g16) = 12
FEATURE [Part::FeaturePython] Screw  label="M3x30-Screw"  # WARN: FeaturePython — macro-defined, semantics opaque (R4)
  Diameter = 4
  Invert = false
  LeftHanded = false
  Length = 11
  LengthCustom = 30
  MatchOuter = false
  OffsetAngle = 0
  Placement = pos=(0,0,22) rot=(0,0,1;0rad)
  Thread = false
  Type = 77
FEATURE [Part::FeaturePython] Nut  label="M3-Nut"  # WARN: FeaturePython — macro-defined, semantics opaque (R4)
  Diameter = 7
  Invert = false
  LeftHanded = false
  MatchOuter = false
  OffsetAngle = 0
  Thread = false
  Type = 19
FEATURE [App::Link] M3x8_Screw  label="M3x25-Screw001"
  LinkPlacement = pos=(105.987,14.07,134.728) rot=(0,1,0;1.5708rad)
  LinkedObject = -> Screw
  Placement = pos=(105.987,14.07,134.728) rot=(0,1,0;1.5708rad)
FEATURE [App::Link] M3_Nut  label="M3-Nut001"
  LinkPlacement = pos=(77.8545,14.07,134.728) rot=(0,1,0;1.5708rad)
  LinkedObject = -> Nut
  Placement = pos=(77.8545,14.07,134.728) rot=(0,1,0;1.5708rad)
FEATURE [Part::FeaturePython] Screw001  label="M3x25-Screw"  # WARN: FeaturePython — macro-defined, semantics opaque (R4)
  Diameter = 4
  Invert = false
  LeftHanded = false
  Length = 11
  LengthCustom = 25
  MatchOuter = false
  OffsetAngle = 0
  Placement = pos=(0,-75,-1) rot=(1,0,0;1.5708rad)
  Thread = false
  Type = 77
FEATURE [App::Link] M3x23_Screw001  label="M3x20-Screw002"
  LinkPlacement = pos=(1.43729,14.07,219.77) rot=(0,0,1;0rad)
  LinkedObject = -> Screw001
  Placement = pos=(1.43729,14.07,219.77) rot=(0,0,1;0rad)
FEATURE [App::Link] M3_Nut001  label="M3-Nut002"
  LinkPlacement = pos=(1.43729,14.07,197.637) rot=(0,0,1;0rad)
  LinkedObject = -> Nut
  Placement = pos=(1.43729,14.07,197.637) rot=(0,0,1;0rad)
FEATURE [Part::FeaturePython] Screw002  label="M3x25-Screw002"  # WARN: FeaturePython — macro-defined, semantics opaque (R4)
  Diameter = 4
  Invert = false
  LeftHanded = false
  Length = 11
  LengthCustom = 25
  MatchOuter = false
  OffsetAngle = 0
  Placement = pos=(0,0,22) rot=(0,0,1;0rad)
  Thread = false
  Type = 77
FEATURE [App::Link] M3_Nut002  label="M3-Nut003"
  LinkPlacement = pos=(-46.4698,14.07,135.22) rot=(0,1,0;4.71239rad)
  LinkedObject = -> Nut
  Placement = pos=(-46.4698,14.07,135.22) rot=(0,1,0;4.71239rad)
FEATURE [App::Link] GY_511_LSM303DLHC001
  LinkPlacement = pos=(3.74739,7.97,135.15) rot=(0.57735,-0.57735,0.57735;2.0944rad)
  LinkedObject = -> GY_511_LSM303DLHC
  Placement = pos=(3.74739,7.97,135.15) rot=(0.57735,-0.57735,0.57735;2.0944rad)
FEATURE [Sketcher::SketchObject] Sketch082
  ArcFitTolerance = 1e-06
  AttachmentSupport = -> [XZ_Plane011]
  ExternalTypes = [0]
  FullyConstrained = true
  MakeInternals = false
  MapMode = 5
  Placement = pos=(0,0,0) rot=(1,0,0;1.5708rad)
  expr: Constraints[1] = VarSet.Base_ring_connector_scew
  sketch-geometry (1):
    g0: Circle CenterX=0 CenterY=0 CenterZ=0 NormalX=0 NormalY=0 NormalZ=1 AngleXU=0 Radius=1.65
  constraints (2):
    c: Coincident(g0,g-1)
    c: Diameter(g0) = 3.3
FEATURE [PartDesign::Pocket] Pocket007
  BaseFeature = -> Mirrored
  Direction = (0,1,-2e-16)
  Length = 5
  Length2 = 5
  Midplane = true
  Profile = -> Sketch082
  ReferenceAxis = -> Sketch082 [N_Axis]
  Refine = true
  Suppressed = false
  Type = 1
FEATURE [PartDesign::Pad] Pad011
  BaseFeature = -> Pocket007
  Direction = (0,0,1)
  Length = 7
  Length2 = 10
  Midplane = true
  Profile = -> Sketch081 [Edge7,Edge6,Edge5,Edge8]
  ReferenceAxis = -> Sketch081 [N_Axis]
  Refine = true
  Suppressed = false
  Type = 0
  expr: Length = VarSet.Base_ring_depth
FEATURE [PartDesign::Pad] Pad012
  BaseFeature = -> Pad011
  Direction = (0,0,1)
  Length = 7
  Length2 = 10
  Midplane = true
  Profile = -> Sketch081 [Edge14,Edge13,Edge15,Edge16]
  ReferenceAxis = -> Sketch081 [N_Axis]
  Refine = true
  Suppressed = false
  Type = 0
  expr: Length = VarSet.Base_ring_depth
FEATURE [PartDesign::Pad] Pad013
  BaseFeature = -> Pad012
  Direction = (0,0,1)
  Length = 4.5
  Length2 = 10
  Profile = -> Sketch081 [Edge12,Edge3,Edge4,Edge9]
  ReferenceAxis = -> Sketch081 [N_Axis]
  Refine = true
  Suppressed = false
  Type = 0
  expr: Length = VarSet.Base_ring_depth / 2 + 1 mm
FEATURE [PartDesign::Pocket] Pocket008
  BaseFeature = -> Pad013
  Direction = (0,0,-1)
  Length = 5
  Length2 = 5
  Midplane = true
  Profile = -> Sketch081 [Edge1,Edge11,Edge2,Edge10]
  ReferenceAxis = -> Sketch081 [N_Axis]
  Refine = true
  Suppressed = false
  Type = 1
FEATURE [PartDesign::Fillet] Fillet
  Base = -> Pocket008 [Edge69,Edge70,Edge83,Edge84]
  BaseFeature = -> Pocket008
  Radius = 2
  Refine = true
  SupportTransform = false
  Suppressed = false
  UseAllEdges = false
FEATURE [PartDesign::Body] Body  label="first_circle"
  AllowCompound = false
  Group = -> [Sketch,Pad002,Sketch069,Pad003,Mirrored,Sketch081,Sketch082,Pocket007,Pad011,Pad012,Pad013,Pocket008,Fillet]
  Origin = -> Origin022
  Tip = -> Fillet
FEATURE [Sketcher::SketchObject] Sketch084
  ArcFitTolerance = 1e-06
  AttachmentSupport = -> [YZ_Plane046]
  ExternalTypes = [0]
  FullyConstrained = true
  MakeInternals = false
  MapMode = 5
  Placement = pos=(0,0,0) rot=(0.57735,0.57735,0.57735;2.0944rad)
  expr: Constraints[1] = VarSet.Base_ring_connector_scew
  sketch-geometry (1):
    g0: Circle CenterX=0 CenterY=0 CenterZ=0 NormalX=0 NormalY=0 NormalZ=1 AngleXU=0 Radius=1.65
  constraints (2):
    c: Coincident(g0,g-1)
    c: Diameter(g0) = 3.3
FEATURE [PartDesign::Pocket] Pocket010
  BaseFeature = -> Pocket003
  Direction = (-1,0,0)
  Length = 5
  Length2 = 5
  Midplane = true
  Profile = -> Sketch084
  ReferenceAxis = -> Sketch084 [N_Axis]
  Refine = true
  Suppressed = false
  Type = 1
FEATURE [App::Link] M3x20_Screw  label="M3x20-Screw003"
  LinkPlacement = pos=(-68.6026,14.07,135.22) rot=(0,1,0;4.71239rad)
  LinkedObject = -> Screw002
  Placement = pos=(-68.6026,14.07,135.22) rot=(0,1,0;4.71239rad)
FEATURE [PartDesign::Fillet] Fillet001
  Base = -> Pocket005 [Edge4,Edge31,Edge36,Edge37]
  BaseFeature = -> Pocket005
  Radius = 2
  Refine = true
  SupportTransform = false
  Suppressed = false
  UseAllEdges = false
FEATURE [PartDesign::Body] Body022  label="third_circle"
  AllowCompound = false
  Group = -> [Sketch074,Sketch075,Sketch076,Pad006,Pad007,Pocket004,Pocket005,Fillet001]
  Origin = -> Origin088
  Tip = -> Fillet001
FEATURE [PartDesign::Fillet] Fillet002
  Base = -> Pocket010 [Edge25,Edge4,Edge30,Edge31]
  BaseFeature = -> Pocket010
  Radius = 2
  Refine = true
  SupportTransform = false
  Suppressed = false
  UseAllEdges = false
FEATURE [PartDesign::Body] Body021  label="second_cicle"
  AllowCompound = false
  Group = -> [Sketch071,Pad004,Pad005,Sketch073,Pocket003,Sketch084,Pocket010,Fillet002]
  Origin = -> Origin086
  Tip = -> Fillet002
FEATURE [App::FeaturePython] Joint  label="Fixed"  # Assembly joint (typed FeaturePython)
  Activated = true
  AngleMax = 0
  AngleMin = 0
  Detach1 = false
  Detach2 = false
  Distance = 0
  Distance2 = 0
  EnableAngleMax = false
  EnableAngleMin = false
  EnableLengthMax = false
  EnableLengthMin = false
  JointType = 0 (Fixed)
  LengthMax = 0
  LengthMin = 0
  Offset2 = pos=(0,0,0) rot=(0,0,-1;1.5708rad)
  Placement1 = pos=(134.728,1.1e-15,7) rot=(0.57735,0.57735,0.57735;4.18879rad)
  Placement2 = pos=(0,7.07,0) rot=(-0.57735,-0.57735,0.57735;2.0944rad)
  Reference1 = -> Assembly [base_outside.Pocket006.Edge18,base_outside.Pocket006.Edge18]
  Reference2 = -> Assembly [base.Pad009.Edge23,base.Pad009.Edge23]
FEATURE [App::FeaturePython] Joint001  label="Fixed001"  # Assembly joint (typed FeaturePython)
  Activated = true
  AngleMax = 0
  AngleMin = 0
  Detach1 = false
  Detach2 = false
  Distance = 0
  Distance2 = 0
  EnableAngleMax = false
  EnableAngleMin = false
  EnableLengthMax = false
  EnableLengthMin = false
  JointType = 0 (Fixed)
  LengthMax = 0
  LengthMin = 0
  Offset2 = pos=(0,0,-3) rot=(0,0,1;0rad)
  Placement1 = pos=(0,0,-2.55) rot=(0,0,1;0rad)
  Placement2 = pos=(0,103.437,-2.41e-14) rot=(-1,0,0;4.71239rad)
  Reference1 = -> Assembly [M3x8_Screw.Face26,M3x8_Screw.Face26]
  Reference2 = -> Assembly [base_outside.Pocket006.Face14,base_outside.Pocket006.Face14]
FEATURE [App::FeaturePython] Joint002  label="Fixed002"  # Assembly joint (typed FeaturePython)
  Activated = true
  AngleMax = 0
  AngleMin = 0
  Detach1 = false
  Detach2 = false
  Distance = 0
  Distance2 = 0
  EnableAngleMax = false
  EnableAngleMin = false
  EnableLengthMax = false
  EnableLengthMin = false
  JointType = 0 (Fixed)
  LengthMax = 0
  LengthMin = 0
  Offset2 = pos=(0,0,-9) rot=(0,0,1;0rad)
  Placement2 = pos=(0,0,-11.55) rot=(0,0,1;0rad)
  Reference1 = -> Assembly [space.Pad010.Face2,space.Pad010.Face2]
  Reference2 = -> Assembly [M3x8_Screw.Face26,M3x8_Screw.Face26]
FEATURE [App::FeaturePython] Joint003  label="Revolute"  # Assembly joint (typed FeaturePython)
  Activated = true
  AngleMax = 0
  AngleMin = 0
  Detach1 = false
  Detach2 = false
  Distance = 0
  Distance2 = 0
  EnableAngleMax = false
  EnableAngleMin = false
  EnableLengthMax = false
  EnableLengthMin = false
  JointType = 1 (Revolute)
  LengthMax = 0
  LengthMin = 0
  Placement1 = pos=(0,92,-1.95e-14) rot=(1,0,0;1.5708rad)
  Placement2 = pos=(0,0,1) rot=(0,0,1;0rad)
  Reference1 = -> Assembly [third_circle.Fillet001.Edge49,third_circle.Fillet001.Edge49]
  Reference2 = -> Assembly [space.Pad010.Edge6,space.Pad010.Edge6]
FEATURE [App::FeaturePython] Joint004  label="Fixed003"  # Assembly joint (typed FeaturePython)
  Activated = true
  AngleMax = 0
  AngleMin = 0
  Detach1 = false
  Detach2 = false
  Distance = 0
  Distance2 = 0
  EnableAngleMax = false
  EnableAngleMin = false
  EnableLengthMax = false
  EnableLengthMin = false
  JointType = 0 (Fixed)
  LengthMax = 0
  LengthMin = 0
  Offset2 = pos=(0,0,-23) rot=(0,0,1;0rad)
  Placement1 = pos=(0,0,0.132804) rot=(0,0,1;0rad)
  Placement2 = pos=(0,0,-28) rot=(0,0,1;0rad)
  Reference1 = -> Assembly [M3_Nut.Edge11,M3_Nut.Edge11]
  Reference2 = -> Assembly [M3x8_Screw.Edge70,M3x8_Screw.Edge70]
FEATURE [App::FeaturePython] Joint005  label="Fixed004"  # Assembly joint (typed FeaturePython)
  Activated = true
  AngleMax = 0
  AngleMin = 0
  Detach1 = false
  Detach2 = false
  Distance = 0
  Distance2 = 0
  EnableAngleMax = false
  EnableAngleMin = false
  EnableLengthMax = false
  EnableLengthMin = false
  JointType = 0 (Fixed)
  LengthMax = 0
  LengthMin = 0
  Offset2 = pos=(0,0,10) rot=(0,0,1;0rad)
  Placement1 = pos=(0,0,-12.55) rot=(0,0,1;0rad)
  Placement2 = pos=(-72.4917,0,0) rot=(0.57735,0.57735,0.57735;2.0944rad)
  Reference1 = -> Assembly [M3x23_Screw001.Face26,M3x23_Screw001.Face26]
  Reference2 = -> Assembly [third_circle.Fillet001.Face18,third_circle.Fillet001.Face18]
FEATURE [App::FeaturePython] Joint006  label="Fixed005"  # Assembly joint (typed FeaturePython)
  Activated = true
  AngleMax = 0
  AngleMin = 0
  Detach1 = false
  Detach2 = false
  Distance = 0
  Distance2 = 0
  EnableAngleMax = false
  EnableAngleMin = false
  EnableLengthMax = false
  EnableLengthMin = false
  JointType = 0 (Fixed)
  LengthMax = 0
  LengthMin = 0
  Offset2 = pos=(0,0,6) rot=(0,0,1;0rad)
  Placement2 = pos=(0,0,-6.55) rot=(0,0,1;0rad)
  Reference1 = -> Assembly [space001.Pad010.Face2,space001.Pad010.Face2]
  Reference2 = -> Assembly [M3x23_Screw001.Face26,M3x23_Screw001.Face26]
FEATURE [App::FeaturePython] Joint007  label="Revolute001"  # Assembly joint (typed FeaturePython)
  Activated = true
  AngleMax = 0
  AngleMin = 0
  Detach1 = false
  Detach2 = false
  Distance = 0
  Distance2 = 0
  EnableAngleMax = false
  EnableAngleMin = false
  EnableLengthMax = false
  EnableLengthMin = false
  JointType = 1 (Revolute)
  LengthMax = 0
  LengthMin = 0
  Placement1 = pos=(77,0,0) rot=(-0.57735,-0.57735,-0.57735;4.18879rad)
  Placement2 = pos=(0,-1.8e-15,-1) rot=(0,0,1;0rad)
  Reference1 = -> Assembly [second_cicle.Fillet002.Edge35,second_cicle.Fillet002.Edge35]
  Reference2 = -> Assembly [space001.Pad010.Edge5,space001.Pad010.Edge5]
FEATURE [App::FeaturePython] Joint008  label="Fixed006"  # Assembly joint (typed FeaturePython)
  Activated = true
  AngleMax = 0
  AngleMin = 0
  Detach1 = false
  Detach2 = false
  Distance = 0
  Distance2 = 0
  EnableAngleMax = false
  EnableAngleMin = false
  EnableLengthMax = false
  EnableLengthMin = false
  JointType = 0 (Fixed)
  LengthMax = 0
  LengthMin = 0
  Offset2 = pos=(0,0,3) rot=(0,0,1;0rad)
  Placement1 = pos=(0,0,0.132804) rot=(0,0,1;0rad)
  Placement2 = pos=(0,0,-22) rot=(0,0,1;0rad)
  Reference1 = -> Assembly [M3_Nut001.Edge11,M3_Nut001.Edge11]
  Reference2 = -> Assembly [M3x23_Screw001.Edge70,M3x23_Screw001.Edge70]
FEATURE [App::FeaturePython] Joint009  label="Fixed007"  # Assembly joint (typed FeaturePython)
  Activated = true
  AngleMax = 0
  AngleMin = 0
  Detach1 = false
  Detach2 = false
  Distance = 0
  Distance2 = 0
  EnableAngleMax = false
  EnableAngleMin = false
  EnableLengthMax = false
  EnableLengthMin = false
  JointType = 0 (Fixed)
  LengthMax = 0
  LengthMin = 0
  Offset2 = pos=(0,0,-10) rot=(0,0,1;0rad)
  Placement1 = pos=(0,-1.8e-15,-12.55) rot=(0,0,1;0rad)
  Placement2 = pos=(4e-16,-57.4899,1.2e-14) rot=(-1,0,0;4.71239rad)
  Reference1 = -> Assembly [M3x20_Screw.Face26,M3x20_Screw.Face26]
  Reference2 = -> Assembly [second_cicle.Fillet002.Face19,second_cicle.Fillet002.Face19]
FEATURE [App::FeaturePython] Joint010  label="Fixed008"  # Assembly joint (typed FeaturePython)
  Activated = true
  AngleMax = 0
  AngleMin = 0
  Detach1 = false
  Detach2 = false
  Distance = 0
  Distance2 = 0
  EnableAngleMax = false
  EnableAngleMin = false
  EnableLengthMax = false
  EnableLengthMin = false
  JointType = 0 (Fixed)
  LengthMax = 0
  LengthMin = 0
  Offset2 = pos=(0,0,6) rot=(0,0,1;0rad)
  Placement2 = pos=(0,-1.8e-15,-6.55) rot=(0,0,1;0rad)
  Reference1 = -> Assembly [space003.Pad010.Face2,space003.Pad010.Face2]
  Reference2 = -> Assembly [M3x20_Screw.Face26,M3x20_Screw.Face26]
FEATURE [App::FeaturePython] Joint011  label="Revolute002"  # Assembly joint (typed FeaturePython)
  Activated = true
  AngleMax = 0
  AngleMin = 0
  Detach1 = false
  Detach2 = false
  Distance = 0
  Distance2 = 0
  EnableAngleMax = false
  EnableAngleMin = false
  EnableLengthMax = false
  EnableLengthMin = false
  JointType = 1 (Revolute)
  LengthMax = 0
  LengthMin = 0
  Reference1 = -> Assembly [M3_Nut002.,M3_Nut002.]
FEATURE [App::FeaturePython] Joint012  label="Fixed009"  # Assembly joint (typed FeaturePython)
  Activated = true
  AngleMax = 0
  AngleMin = 0
  Detach1 = false
  Detach2 = false
  Distance = 0
  Distance2 = 0
  EnableAngleMax = false
  EnableAngleMin = false
  EnableLengthMax = false
  EnableLengthMin = false
  JointType = 0 (Fixed)
  LengthMax = 0
  LengthMin = 0
  Offset2 = pos=(0,0,3) rot=(0,0,1;0rad)
  Placement1 = pos=(0,0,0.132804) rot=(0,0,1;0rad)
  Placement2 = pos=(0,0,-22) rot=(0,0,1;0rad)
  Reference1 = -> Assembly [M3_Nut002.Edge11,M3_Nut002.Edge11]
  Reference2 = -> Assembly [M3x20_Screw.Edge70,M3x20_Screw.Edge70]
FEATURE [App::FeaturePython] Joint013  label="Fixed010"  # Assembly joint (typed FeaturePython)
  Activated = true
  AngleMax = 0
  AngleMin = 0
  Detach1 = false
  Detach2 = false
  Distance = 0
  Distance2 = 0
  EnableAngleMax = false
  EnableAngleMin = false
  EnableLengthMax = false
  EnableLengthMin = false
  JointType = 0 (Fixed)
  LengthMax = 0
  LengthMin = 0
  Placement1 = pos=(7.62,5.2,-1.6) rot=(0,0,1;0rad)
  Placement2 = pos=(7.55,2.4,4.5) rot=(0,0,1;0rad)
  Reference1 = -> Assembly [GY_511_LSM303DLHC001.Part__Feature001.Edge14,GY_511_LSM303DLHC001.Part__Feature001.Edge14]
  Reference2 = -> Assembly [first_circle.Fillet.Edge113,first_circle.Fillet.Edge113]
FEATURE [Assembly::JointGroup] Joints
  Group = -> [GroundedJoint,Joint,Joint001,Joint002,Joint003,Joint004,Joint005,Joint006,Joint007,Joint008,Joint009,Joint010,Joint011,Joint012,Joint013]
FEATURE [Assembly::AssemblyObject] Assembly
  Group = -> [Joints,base,GroundedJoint,base_outside,space,third_circle,space001,space002,space003,second_cicle,first_circle,space004,M3x8_Screw,M3_Nut,M3x23_Screw001,M3_Nut001,M3_Nut002,GY_511_LSM303DLHC001,M3x20_Screw,Joint,Joint001,Joint002,Joint003,Joint004,Joint005,Joint006,Joint007,Joint008,Joint009,Joint010,Joint011,Joint012,Joint013]
  Origin = -> Origin096
  Type = Assembly
